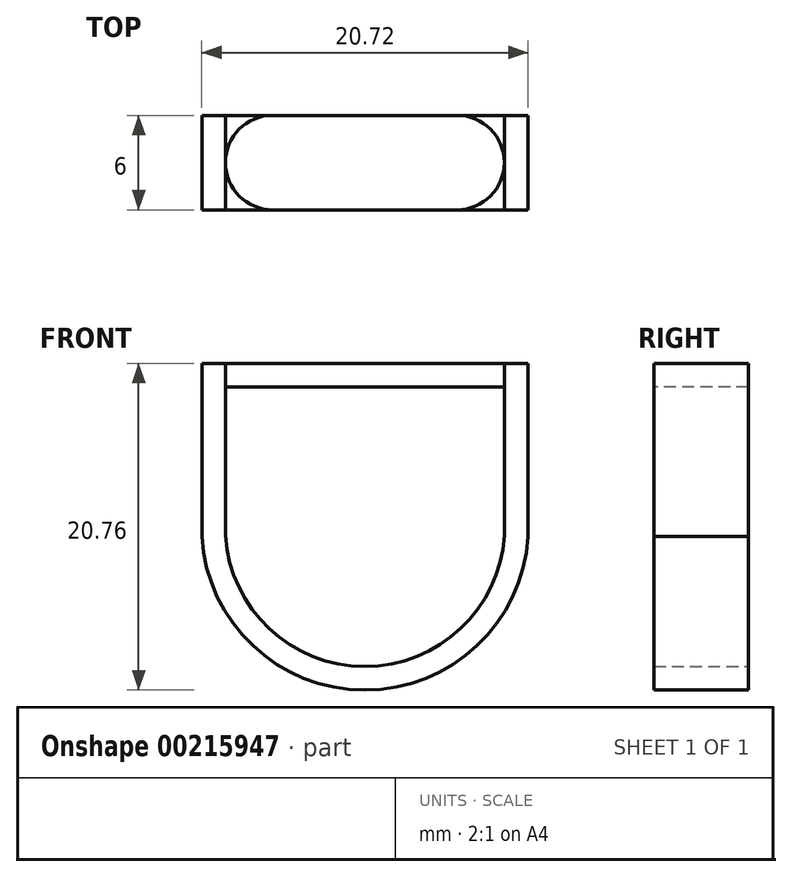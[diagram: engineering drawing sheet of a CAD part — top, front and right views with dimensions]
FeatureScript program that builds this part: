
annotation { "Feature Type Name" : "Feature", "Feature Type Description" : "" }
export const myFeature = defineFeature(function(context is Context, id is Id, definition is map)
    precondition{}
    {
        {
            var Q0;
            Q0=qCreatedBy(makeId("Front.planeOp"),FACE);
            var sketch = newSketch(context, id + "F0", { "sketchPlane" : qUnion([Q0])});
            skArc(sketch, "E0", {"start": v(-8.86, -0.56) * mm, "mid": v(0, -8.88) * mm, "end": v(8.86, -0.56) * mm});
            skArc(sketch, "E1.0", {"start": v(-10.36, -0.61) * mm, "mid": v(0, -10.37) * mm, "end": v(10.36, -0.61) * mm});
            skLineSegment(sketch, "E2.bottom", {"start": v(8.86, 8.88) * mm, "end": v(0.62, 8.88) * mm});
            skLineSegment(sketch, "E2.top", {"start": v(8.86, 10.38) * mm, "end": v(-8.86, 10.38) * mm});
            skLineSegment(sketch, "E2.left", {"start": v(8.86, 8.88) * mm, "end": v(8.86, 10.38) * mm});
            skLineSegment(sketch, "E2.right", {"start": v(-8.86, 8.88) * mm, "end": v(-8.86, 10.38) * mm});
            skPoint(sketch, "E2.middle", {"position": v(0, 9.63) * mm});
            skLineSegment(sketch, "E3", {"start": v(-10.36, -0.61) * mm, "end": v(-10.36, 8.88) * mm});
            skLineSegment(sketch, "E4.MirrorCS", {"start": v(10.36, -0.61) * mm, "end": v(10.36, 8.88) * mm});
            skLineSegment(sketch, "E5.0", {"start": v(8.86, -0.56) * mm, "end": v(8.86, 8.88) * mm});
            skLineSegment(sketch, "E6.MirrorCS", {"start": v(-8.86, -0.56) * mm, "end": v(-8.86, 8.88) * mm});
            skLineSegment(sketch, "E7", {"start": v(-8.86, 10.38) * mm, "end": v(-10.36, 10.38) * mm});
            skLineSegment(sketch, "E8", {"start": v(-10.36, 10.38) * mm, "end": v(-10.36, 8.88) * mm});
            skLineSegment(sketch, "E9", {"start": v(8.86, 10.38) * mm, "end": v(10.36, 10.38) * mm});
            skLineSegment(sketch, "E10", {"start": v(10.36, 10.38) * mm, "end": v(10.36, 8.88) * mm});
            skLineSegment(sketch, "E11.trimOffspring", {"start": v(-0.62, 8.88) * mm, "end": v(-8.86, 8.88) * mm});
            skLineSegment(sketch, "E12", {"start": v(0.62, 8.88) * mm, "end": v(-0.62, 8.88) * mm});
            skCircle(sketch, "E13", {"center": v(0, 0) * mm, "radius": 8.88 * mm, "construction": true});
            skSolve(sketch);
        }
        {
            var Q0;
            {var subQ3=sQuery(id+"F0.wireOp",EDGE,"E5.0");var subQ7=sQuery(id+"F0.wireOp",EDGE,"E0");var subQ8=makeQuery(id+"F0.imprint","INTERSECT",VERTEX,{"derivedFrom":[subQ7,subQ3]});Q0=makeQuery(id+"F0.imprint","IMPRINT",FACE,{"disambiguationData":[TD([[makeQuery(id+"F0.imprint","IMPRINT",EDGE,{"disambiguationData":[TD([[subQ8,1.0]])],"derivedFrom":subQ7}),-1.0]])]});}
            var Q1;
            {var subQ0=sQuery(id+"F0.wireOp",EDGE,"E4.MirrorCS");Q1=makeQuery(id+"F0.imprint","IMPRINT",FACE,{"disambiguationData":[TD([[makeQuery(id+"F0.imprint","IMPRINT",EDGE,{"derivedFrom":subQ0}),1.0]])]});}
            var Q2;
            {var subQ0=sQuery(id+"F0.wireOp",EDGE,"E3");Q2=makeQuery(id+"F0.imprint","IMPRINT",FACE,{"disambiguationData":[TD([[makeQuery(id+"F0.imprint","IMPRINT",EDGE,{"derivedFrom":subQ0}),-1.0]])]});}
            extrude(context, id + "F1", {"entities" : qUnion([Q0, Q1, Q2]), "depth" : 3 * mm, "hasSecondDirection" : true, "secondDirectionOppositeDirection" : true, "secondDirectionDepth" : 3 * mm});
        }
        {
            var Q0;
            Q0=makeQuery(id+"F0.imprint","IMPRINT",FACE,{"disambiguationData":[TD([[makeQuery(id+"F0.imprint","IMPRINT",EDGE,{"derivedFrom":sQuery(id+"F0.wireOp",EDGE,"E2.top")}),1.0]])]});
            extrude(context, id + "F2", {"entities" : qUnion([Q0]), "depth" : 3 * mm, "hasSecondDirection" : true, "secondDirectionOppositeDirection" : true, "secondDirectionDepth" : 3 * mm});
        }
        {
            var Q0;
            Q0=makeQuery(id+"F2.opExtrude","CAP_EDGE",EDGE,{"disambiguationData":[OSD([sQuery(id+"F0.wireOp",EDGE,"E2.right")])],"isStart":false});
            var Q1;
            Q1=makeQuery(id+"F2.opExtrude","CAP_EDGE",EDGE,{"disambiguationData":[OSD([sQuery(id+"F0.wireOp",EDGE,"E2.right")])],"isStart":true});
            var Q2;
            Q2=makeQuery(id+"F2.opExtrude","CAP_EDGE",EDGE,{"disambiguationData":[OSD([sQuery(id+"F0.wireOp",EDGE,"E2.left")])],"isStart":false});
            var Q3;
            Q3=makeQuery(id+"F2.opExtrude","CAP_EDGE",EDGE,{"disambiguationData":[OSD([sQuery(id+"F0.wireOp",EDGE,"E2.left")])],"isStart":true});
            fillet(context, id + "F3", {"entities" : qUnion([Q0, Q1, Q2, Q3]), "radius" : 3 * mm, "tangentPropagation" : true, "allowEdgeOverflow" : false});
        }
    });
